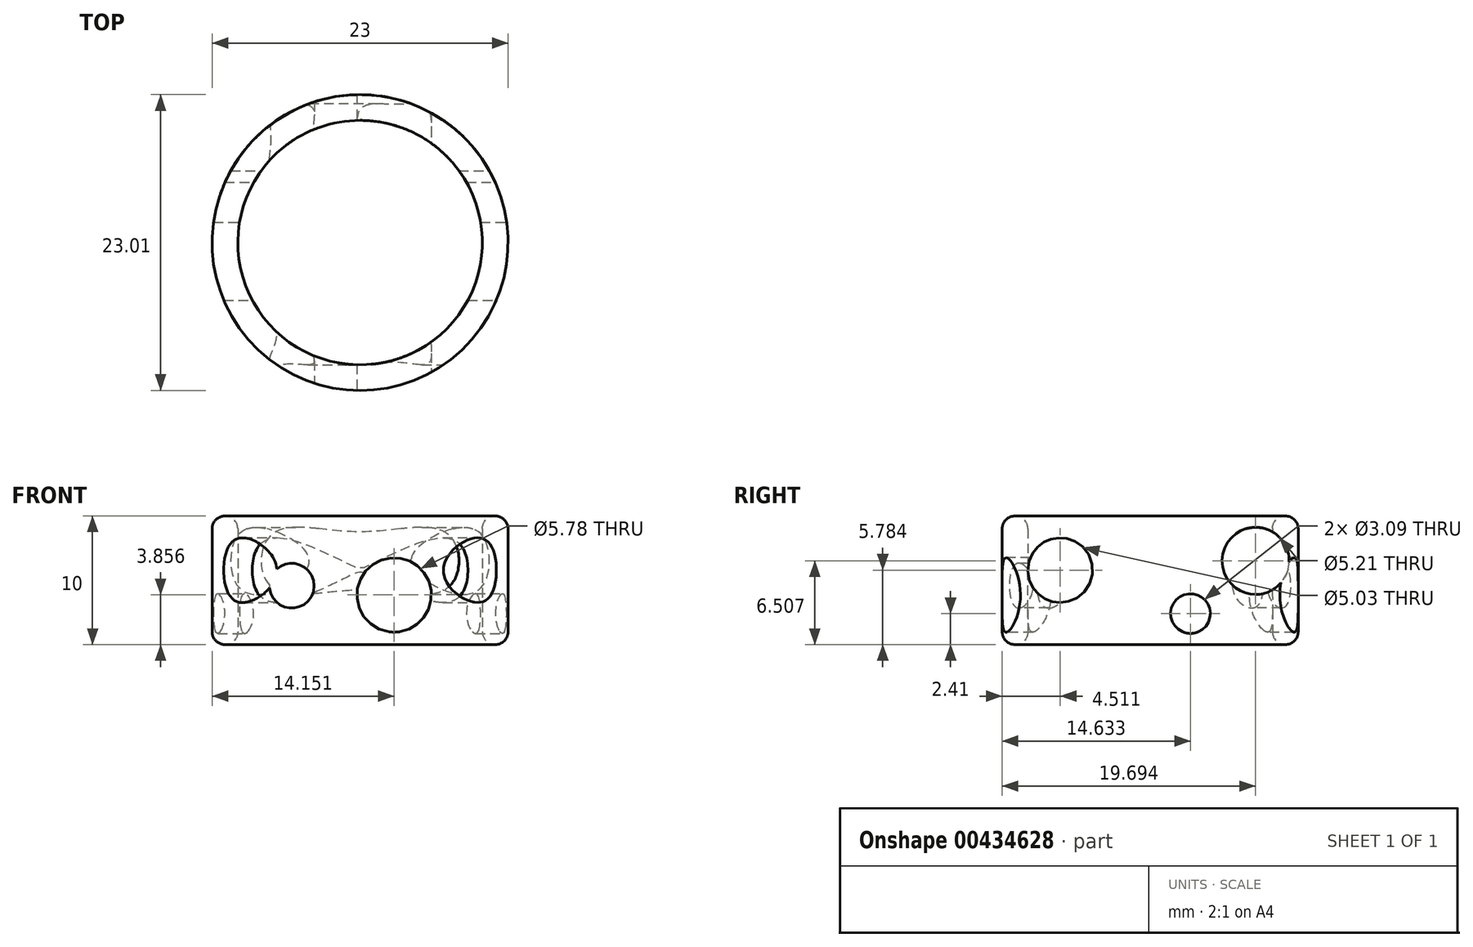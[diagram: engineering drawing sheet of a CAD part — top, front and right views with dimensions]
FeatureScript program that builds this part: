
annotation { "Feature Type Name" : "Feature", "Feature Type Description" : "" }
export const myFeature = defineFeature(function(context is Context, id is Id, definition is map)
    precondition{}
    {
        {
            var Q0;
            Q0=qCreatedBy(makeId("Top.planeOp"),FACE);
            var sketch = newSketch(context, id + "F0", { "sketchPlane" : qUnion([Q0])});
            skCircle(sketch, "E0", {"center": v(0, 0) * mm, "radius": 9.5 * mm});
            skCircle(sketch, "E1", {"center": v(0, 0) * mm, "radius": 11.5 * mm});
            skSolve(sketch);
        }
        {
            var Q0;
            Q0=makeQuery(id+"F0.imprint","IMPRINT",FACE,{"disambiguationData":[TD([[makeQuery(id+"F0.imprint","IMPRINT",EDGE,{"derivedFrom":sQuery(id+"F0.wireOp",EDGE,"E0")}),-1.0]])]});
            extrude(context, id + "F1", {"entities" : qUnion([Q0]), "depth" : 10 * mm});
        }
        {
            var Q0;
            Q0=makeQuery(id+"F1.opExtrude","CAP_EDGE",EDGE,{"disambiguationData":[OSD([sQuery(id+"F0.wireOp",EDGE,"E1")])],"isStart":false});
            var Q1;
            Q1=makeQuery(id+"F1.opExtrude","CAP_EDGE",EDGE,{"disambiguationData":[OSD([sQuery(id+"F0.wireOp",EDGE,"E0")])],"isStart":false});
            var Q2;
            Q2=makeQuery(id+"F1.opExtrude","CAP_EDGE",EDGE,{"disambiguationData":[OSD([sQuery(id+"F0.wireOp",EDGE,"E0")])],"isStart":true});
            var Q3;
            Q3=makeQuery(id+"F1.opExtrude","CAP_EDGE",EDGE,{"disambiguationData":[OSD([sQuery(id+"F0.wireOp",EDGE,"E1")])],"isStart":true});
            fillet(context, id + "F2", {"entities" : qUnion([Q0, Q1, Q2, Q3]), "radius" : 1 * mm, "tangentPropagation" : true, "allowEdgeOverflow" : false});
        }
        {
            var Q0;
            Q0=qCreatedBy(makeId("Right.planeOp"),FACE);
            cPlane(context, id + "F3", {"entities" : qUnion([Q0]), "cplaneType" : CPlaneType.OFFSET, "offset" : 25.4 * mm, "width" : 152.4 * mm, "height" : 152.4 * mm});
        }
        {
            var Q0;
            Q0=qCreatedBy(id+"F3.planeOp",FACE);
            var sketch = newSketch(context, id + "F4", { "sketchPlane" : qUnion([Q0])});
            skCircle(sketch, "E2", {"center": v(-6.99, 5.78) * mm, "radius": 2.52 * mm});
            skCircle(sketch, "E3", {"center": v(3.13, 2.4) * mm, "radius": 1.54 * mm});
            skCircle(sketch, "E4", {"center": v(8.2, 6.5) * mm, "radius": 2.6 * mm});
            skSolve(sketch);
        }
        {
            var Q0;
            Q0=makeQuery(id+"F4.imprint","IMPRINT",FACE,{"disambiguationData":[TD([[makeQuery(id+"F4.imprint","IMPRINT",EDGE,{"derivedFrom":sQuery(id+"F4.wireOp",EDGE,"E2")}),1.0]])]});
            var Q1;
            Q1=makeQuery(id+"F4.imprint","IMPRINT",FACE,{"disambiguationData":[TD([[makeQuery(id+"F4.imprint","IMPRINT",EDGE,{"derivedFrom":sQuery(id+"F4.wireOp",EDGE,"E3")}),1.0]])]});
            var Q2;
            Q2=makeQuery(id+"F4.imprint","IMPRINT",FACE,{"disambiguationData":[TD([[makeQuery(id+"F4.imprint","IMPRINT",EDGE,{"derivedFrom":sQuery(id+"F4.wireOp",EDGE,"E4")}),1.0]])]});
            extrude(context, id + "F5", {"entities" : qUnion([Q0, Q1, Q2]), "operationType" : NewBodyOperationType.REMOVE, "oppositeDirection" : true, "depth" : 50.8 * mm});
        }
        {
            var Q0;
            Q0=qCreatedBy(makeId("Front.planeOp"),FACE);
            cPlane(context, id + "F6", {"entities" : qUnion([Q0]), "cplaneType" : CPlaneType.OFFSET, "offset" : 25.4 * mm, "width" : 152.4 * mm, "height" : 152.4 * mm});
        }
        {
            var Q0;
            Q0=qCreatedBy(id+"F6.planeOp",FACE);
            var sketch = newSketch(context, id + "F7", { "sketchPlane" : qUnion([Q0])});
            skCircle(sketch, "E5", {"center": v(-5.3, 4.58) * mm, "radius": 1.74 * mm});
            skCircle(sketch, "E6", {"center": v(2.65, 3.86) * mm, "radius": 2.9 * mm});
            skSolve(sketch);
        }
        {
            var Q0;
            Q0=makeQuery(id+"F7.imprint","IMPRINT",FACE,{"disambiguationData":[TD([[makeQuery(id+"F7.imprint","IMPRINT",EDGE,{"derivedFrom":sQuery(id+"F7.wireOp",EDGE,"E6")}),1.0]])]});
            var Q1;
            Q1=makeQuery(id+"F7.imprint","IMPRINT",FACE,{"disambiguationData":[TD([[makeQuery(id+"F7.imprint","IMPRINT",EDGE,{"derivedFrom":sQuery(id+"F7.wireOp",EDGE,"E5")}),1.0]])]});
            extrude(context, id + "F8", {"entities" : qUnion([Q0, Q1]), "operationType" : NewBodyOperationType.REMOVE, "oppositeDirection" : true, "depth" : 50.8 * mm});
        }
    });
